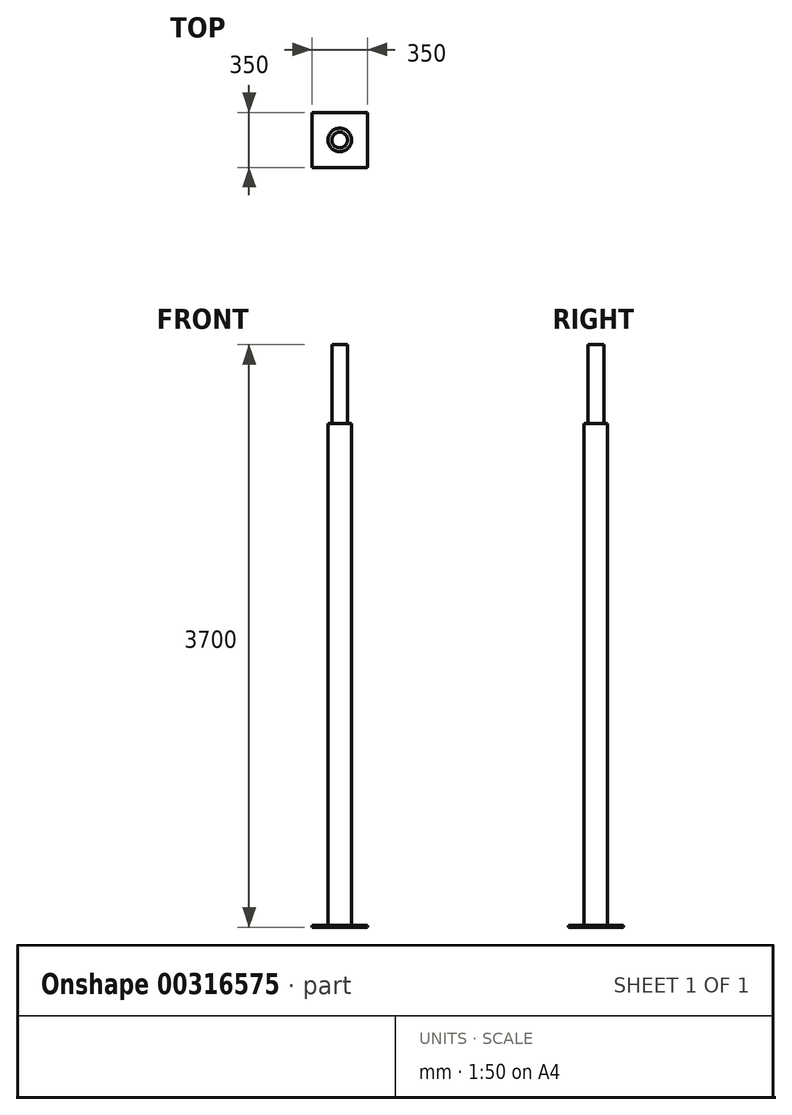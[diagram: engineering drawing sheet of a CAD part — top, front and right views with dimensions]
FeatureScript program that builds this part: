
annotation { "Feature Type Name" : "Feature", "Feature Type Description" : "" }
export const myFeature = defineFeature(function(context is Context, id is Id, definition is map)
    precondition{}
    {
        {
            var Q0;
            Q0=qCreatedBy(makeId("Top.planeOp"),FACE);
            var sketch = newSketch(context, id + "F0", { "sketchPlane" : qUnion([Q0])});
            skLineSegment(sketch, "E0.bottom", {"start": v(175, -175) * mm, "end": v(-175, -175) * mm});
            skLineSegment(sketch, "E0.top", {"start": v(175, 175) * mm, "end": v(-175, 175) * mm});
            skLineSegment(sketch, "E0.left", {"start": v(175, -175) * mm, "end": v(175, 175) * mm});
            skLineSegment(sketch, "E0.right", {"start": v(-175, -175) * mm, "end": v(-175, 175) * mm});
            skPoint(sketch, "E0.middle", {"position": v(0, 0) * mm});
            skSolve(sketch);
        }
        {
            var Q0;
            Q0=makeQuery(id+"F0.imprint","IMPRINT",FACE,{"disambiguationData":[TD([[makeQuery(id+"F0.imprint","IMPRINT",EDGE,{"derivedFrom":sQuery(id+"F0.wireOp",EDGE,"E0.bottom")}),-1.0]])]});
            extrude(context, id + "F1", {"entities" : qUnion([Q0]), "depth" : 10 * mm});
        }
        {
            var Q0;
            Q0=makeQuery(id+"F1.opExtrude","CAP_FACE",FACE,{"disambiguationData":[OSD([sQuery(id+"F0.wireOp",EDGE,"E0.bottom"),sQuery(id+"F0.wireOp",EDGE,"E0.top"),sQuery(id+"F0.wireOp",EDGE,"E0.left"),sQuery(id+"F0.wireOp",EDGE,"E0.right")])],"isStart":false});
            var sketch = newSketch(context, id + "F2", { "sketchPlane" : qUnion([Q0])});
            skCircle(sketch, "E1", {"center": v(0, 0) * mm, "radius": 75 * mm});
            skSolve(sketch);
        }
        {
            var Q0;
            Q0=makeQuery(id+"F2.imprint","IMPRINT",FACE,{"disambiguationData":[TD([[makeQuery(id+"F2.imprint","IMPRINT",EDGE,{"derivedFrom":sQuery(id+"F2.wireOp",EDGE,"E1")}),1.0]])]});
            extrude(context, id + "F3", {"entities" : qUnion([Q0]), "operationType" : NewBodyOperationType.ADD, "depth" : 3690 * mm});
        }
        {
            var Q0;
            Q0=makeQuery(id+"F3.opExtrude","CAP_FACE",FACE,{"disambiguationData":[OSD([sQuery(id+"F2.wireOp",EDGE,"E1")])],"isStart":false});
            var sketch = newSketch(context, id + "F4", { "sketchPlane" : qUnion([Q0])});
            skCircle(sketch, "E2", {"center": v(0, 0) * mm, "radius": 50 * mm});
            skSolve(sketch);
        }
        {
            var Q0;
            Q0=makeQuery(id+"F4.imprint","IMPRINT",FACE,{"disambiguationData":[TD([[makeQuery(id+"F4.imprint","IMPRINT",EDGE,{"derivedFrom":sQuery(id+"F4.wireOp",EDGE,"E2")}),-1.0]])]});
            extrude(context, id + "F5", {"entities" : qUnion([Q0]), "operationType" : NewBodyOperationType.REMOVE, "oppositeDirection" : true, "depth" : 500 * mm});
        }
    });
